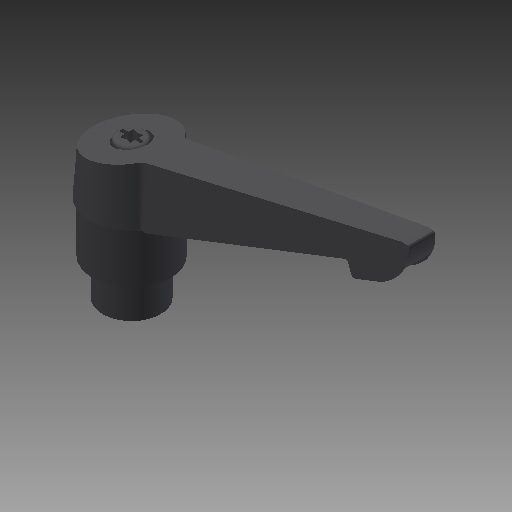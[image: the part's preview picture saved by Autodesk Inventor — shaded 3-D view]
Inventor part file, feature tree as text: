
AUTODESK INVENTOR PART (.ipt)
format: ipt  version: 2018 (Build 220112000, 112)  size: 202,240 bytes
history: native  units: mm
features: sketch x11, extrude x7, other x7, revolve x3, hole x1
ambient origin geometry x8: Origin, YZ Plane, XZ Plane, XY Plane, X Axis, Y Axis, Z Axis, Center Point
bodies: Solid1 (feature_tree)
feature tree (29):
  revolve  "Revolution1"  Angle=360.0deg
  revolve  "Revolution2"  [1 undecoded]
  extrude  "Extrusion1"  TaperAngle=360.0deg  [1 undecoded]
  extrude  "Extrusion2"  Depth=7.0mm TaperAngle=0.0deg
  extrude  "Extrusion3"  Depth=10.0mm TaperAngle=0.0deg
  revolve  "Revolution3"  [1 undecoded]
  extrude  "Extrusion4"  [1 undecoded]
  extrude  "Extrusion5"  [1 undecoded]
  extrude  "Extrusion6"  [1 undecoded]
  extrude  "Extrusion7"  [1 undecoded]
  hole  "Drilling 2"  [1 undecoded]
  other  "fluegel_XY"
  other  "fluegel_YZ"
  other  "fluegel_ZX"
  other  "fluegel_X"
  other  "fluegel_Y"
  other  "fluegel_Z"
  other  "fluegel_Center"
  sketch  "Skizze_1"  dims[d0=360.0deg d1=360.0deg]
  sketch  "Skizze_2"  dims[d2=30.0mm d3=-0.663225mm d4=50.0mm d5=0.0mm]
  sketch  "Skizze_4"  dims[d9=3.0mm d10=0.0mm d11=7.0mm d12=0.0mm]
  sketch  "Skizze_3"  dims[d6=25.0mm d7=0.0mm d8=360.0deg]
  sketch  "Skizze_5"  dims[d13=6.0mm d14=0.0mm d15=10.0mm d16=0.0mm]
  sketch  "Skizze_6"  dims[d17=8.376mm d18=14.0mm d19=10.0mm d20=2.0mm d21=15.707963mm d22=14.0mm d23=0.0mm]
  sketch  "Skizze_7"
  sketch  "Skizze_12"
  sketch  "Skizze_13"
  sketch  "Skizze_14"
  sketch  "Sketch11"
note: 8 required parameter values undecoded (feature->parameter linkage not recoverable at this tier; creation-order binding heuristic only, values carry confidence <= 0.55)